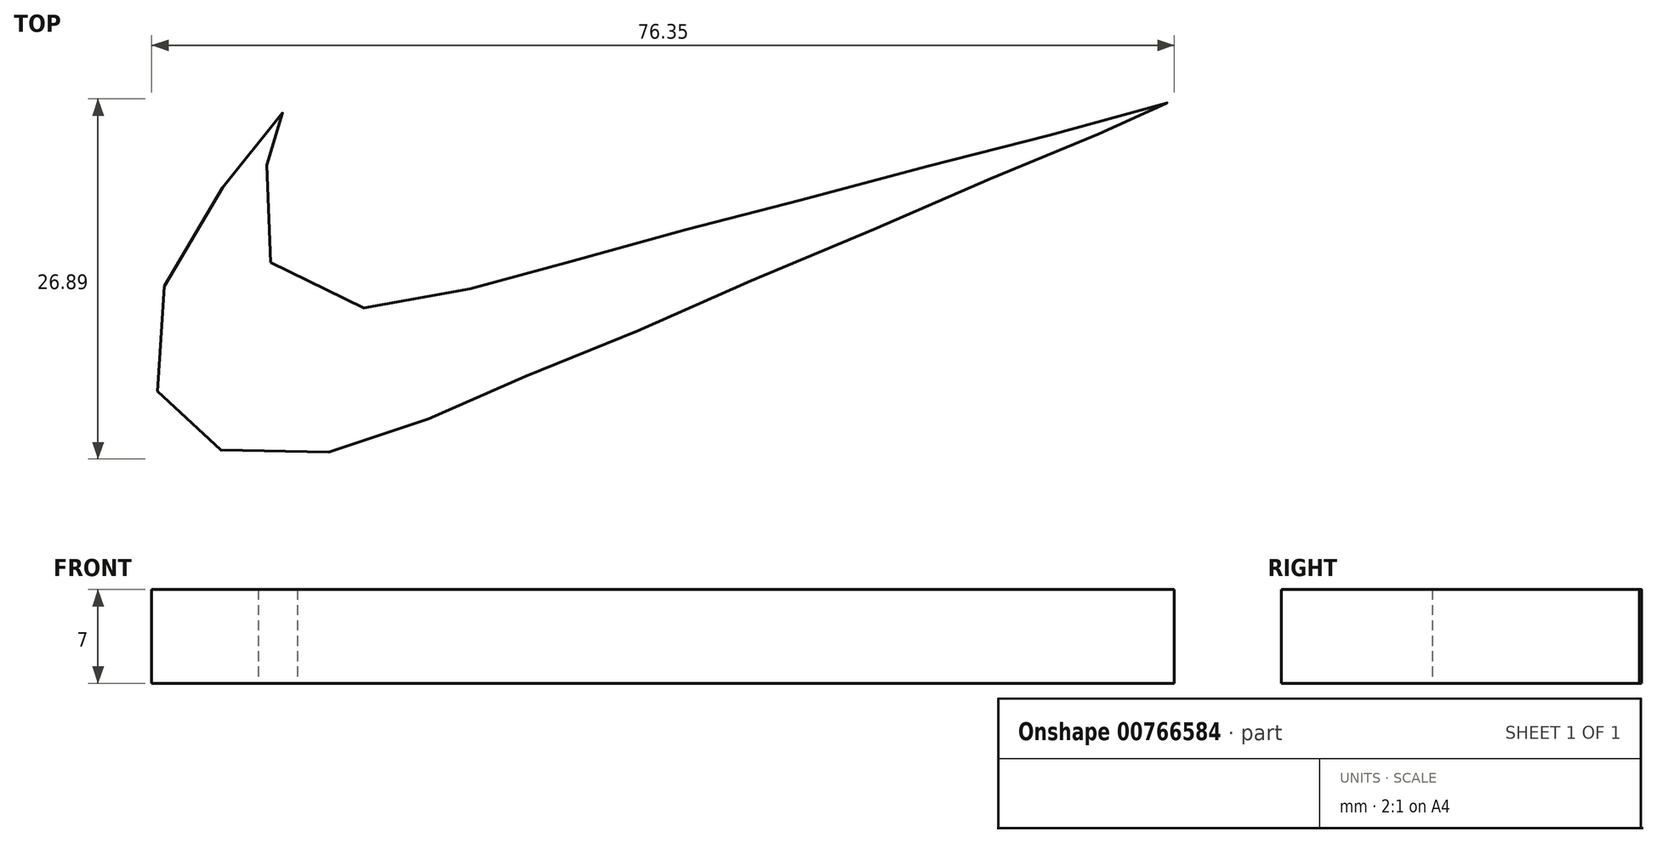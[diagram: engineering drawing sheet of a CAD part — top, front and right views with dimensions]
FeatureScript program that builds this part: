
annotation { "Feature Type Name" : "Feature", "Feature Type Description" : "" }
export const myFeature = defineFeature(function(context is Context, id is Id, definition is map)
    precondition{}
    {
        {
            var Q0;
            Q0=qCreatedBy(makeId("Top.planeOp"),FACE);
            var sketch = newSketch(context, id + "F0", { "sketchPlane" : qUnion([Q0])});
            skFitSpline(sketch, "E0", {"points": [v(-71.05, 19.91) * mm, v(-70.03, 18.34) * mm, v(-67.79, 17.04) * mm, v(-62.64, 16.53) * mm, v(-59.77, 17) * mm, v(-57.02, 17.71) * mm, v(-54.39, 18.42) * mm, v(-51.67, 19.13) * mm, v(-48.77, 19.95) * mm, v(-45.54, 20.86) * mm, v(-41.65, 21.96) * mm, v(-37.84, 22.9) * mm, v(-34.42, 23.76) * mm, v(-30.32, 24.9) * mm, v(-25.6, 26.12) * mm, v(-21.77, 27.2) * mm, v(-17.65, 28.27) * mm, v(-13.68, 29.2) * mm, v(-9.2, 30.46) * mm, v(-6.2, 31.26) * mm, v(-3.59, 31.96) * mm, v(-5.55, 31.12) * mm, v(-7.7, 30.18) * mm, v(-10.6, 28.97) * mm, v(-13.45, 27.8) * mm, v(-17.33, 26.16) * mm, v(-20.5, 24.67) * mm, v(-25.08, 22.8) * mm, v(-29.06, 21.02) * mm, v(-33.6, 19.25) * mm, v(-37.94, 17.28) * mm, v(-41.4, 15.79) * mm, v(-45.18, 14.2) * mm, v(-48.97, 12.7) * mm, v(-52.24, 11.35) * mm, v(-55.23, 10.04) * mm, v(-57.61, 9.06) * mm, v(-60.28, 7.8) * mm, v(-62.47, 7.05) * mm, v(-65.46, 6.07) * mm, v(-69.5, 5.36) * mm, v(-72.6, 5.32) * mm, v(-74.98, 5.98) * mm, v(-77, 7) * mm, v(-78.33, 8.36) * mm, v(-79.43, 10.13) * mm, v(-79.92, 12.6) * mm, v(-79.7, 15.77) * mm, v(-78.68, 18.95) * mm, v(-77.27, 21.86) * mm, v(-75.02, 24.95) * mm, v(-73.35, 27.5) * mm, v(-71.8, 29.1) * mm, v(-70.48, 30.73) * mm, v(-69.07, 32.14) * mm, v(-70.08, 30.42) * mm, v(-71.23, 27.73) * mm, v(-71.85, 24.6) * mm, v(-71.94, 22.4) * mm, v(-71.05, 19.91) * mm]});
            skSolve(sketch);
        }
        {
            var Q0;
            Q0 = qSketchRegion(id + "F0", true);
            extrude(context, id + "F1", {"entities" : qUnion([Q0]), "depth" : 7 * mm, "offsetDistance" : 25.4 * mm});
        }
    });
